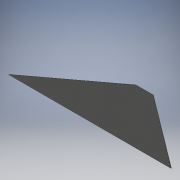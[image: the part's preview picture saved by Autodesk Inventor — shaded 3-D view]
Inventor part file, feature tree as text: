
AUTODESK INVENTOR PART (.ipt)
format: ipt  version: 2017 SP1 (Build 210196100, 196)  size: 97,280 bytes
history: native  units: in
note: dims shown in document units (in); Inventor stores cm internally (conversion verified against a paired STEP export)
features: extrude x1, sketch x1
ambient origin geometry x8: Origin, YZ Plane, XZ Plane, XY Plane, X Axis, Y Axis, Z Axis, Center Point
bodies: Solid1 (feature_tree)
feature tree (2):
  extrude  "Extrusion1"  Depth=0.0625in
  sketch  "Sketch1"  dims[d0=24.17in d1=18.88in d2=8.09in d3=2.6in d4=0.0625in d5=0.0in]
